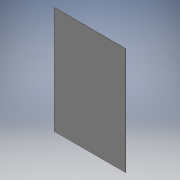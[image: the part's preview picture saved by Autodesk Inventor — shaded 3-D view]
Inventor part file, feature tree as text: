
AUTODESK INVENTOR PART (.ipt)
format: ipt  version: 2016 (Build 200138000, 138)  size: 86,016 bytes
history: native  units: mm
features: other x1, extrude x1, sketch x1
ambient origin geometry x8: Origin, YZ Plane, XZ Plane, XY Plane, X Axis, Y Axis, Z Axis, Center Point
bodies: Body1 (feature_tree)
feature tree (3):
  other  "ソリッド1"
  extrude  "押し出し1"  Depth=400.0mm
  sketch  "スケッチ1"
